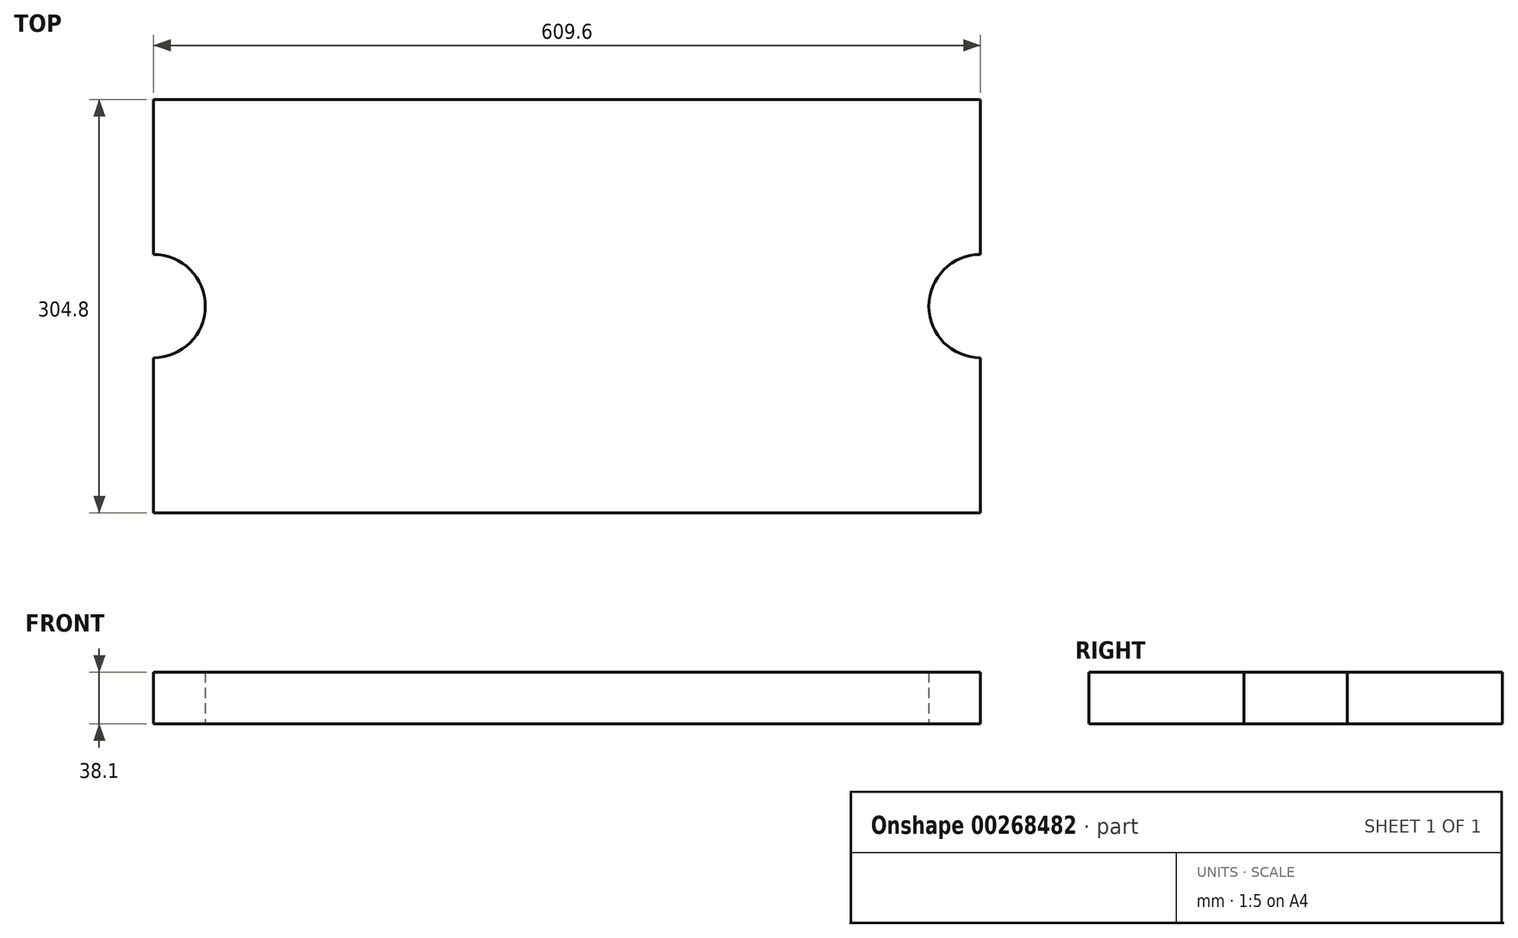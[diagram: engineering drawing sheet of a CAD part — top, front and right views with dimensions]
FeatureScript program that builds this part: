
annotation { "Feature Type Name" : "Feature", "Feature Type Description" : "" }
export const myFeature = defineFeature(function(context is Context, id is Id, definition is map)
    precondition{}
    {
        {
            var Q0;
            Q0=qCreatedBy(makeId("Top.planeOp"),FACE);
            var sketch = newSketch(context, id + "F0", { "sketchPlane" : qUnion([Q0])});
            skLineSegment(sketch, "E0.bottom", {"start": v(304.8, -152.4) * mm, "end": v(-304.8, -152.4) * mm});
            skLineSegment(sketch, "E0.top", {"start": v(304.8, 152.4) * mm, "end": v(-304.8, 152.4) * mm});
            skLineSegment(sketch, "E0.left", {"start": v(304.8, -152.4) * mm, "end": v(304.8, 152.4) * mm});
            skLineSegment(sketch, "E0.right", {"start": v(-304.8, -152.4) * mm, "end": v(-304.8, 152.4) * mm});
            skPoint(sketch, "E0.middle", {"position": v(0, 0) * mm});
            skArc(sketch, "E1", {"start": v(-304.8, -38.1) * mm, "mid": v(-266.7, 0) * mm, "end": v(-304.8, 38.1) * mm});
            skArc(sketch, "E2", {"start": v(304.8, 38.1) * mm, "mid": v(266.7, 0) * mm, "end": v(304.8, -38.1) * mm});
            skSolve(sketch);
        }
        {
            var Q0;
            {var subQ3=sQuery(id+"F0.wireOp",EDGE,"E0.bottom");Q0=makeQuery(id+"F0.imprint","IMPRINT",FACE,{"disambiguationData":[TD([[makeQuery(id+"F0.imprint","IMPRINT",EDGE,{"derivedFrom":subQ3}),-1.0]])]});}
            extrude(context, id + "F1", {"entities" : qUnion([Q0]), "depth" : 38.1 * mm});
        }
    });
